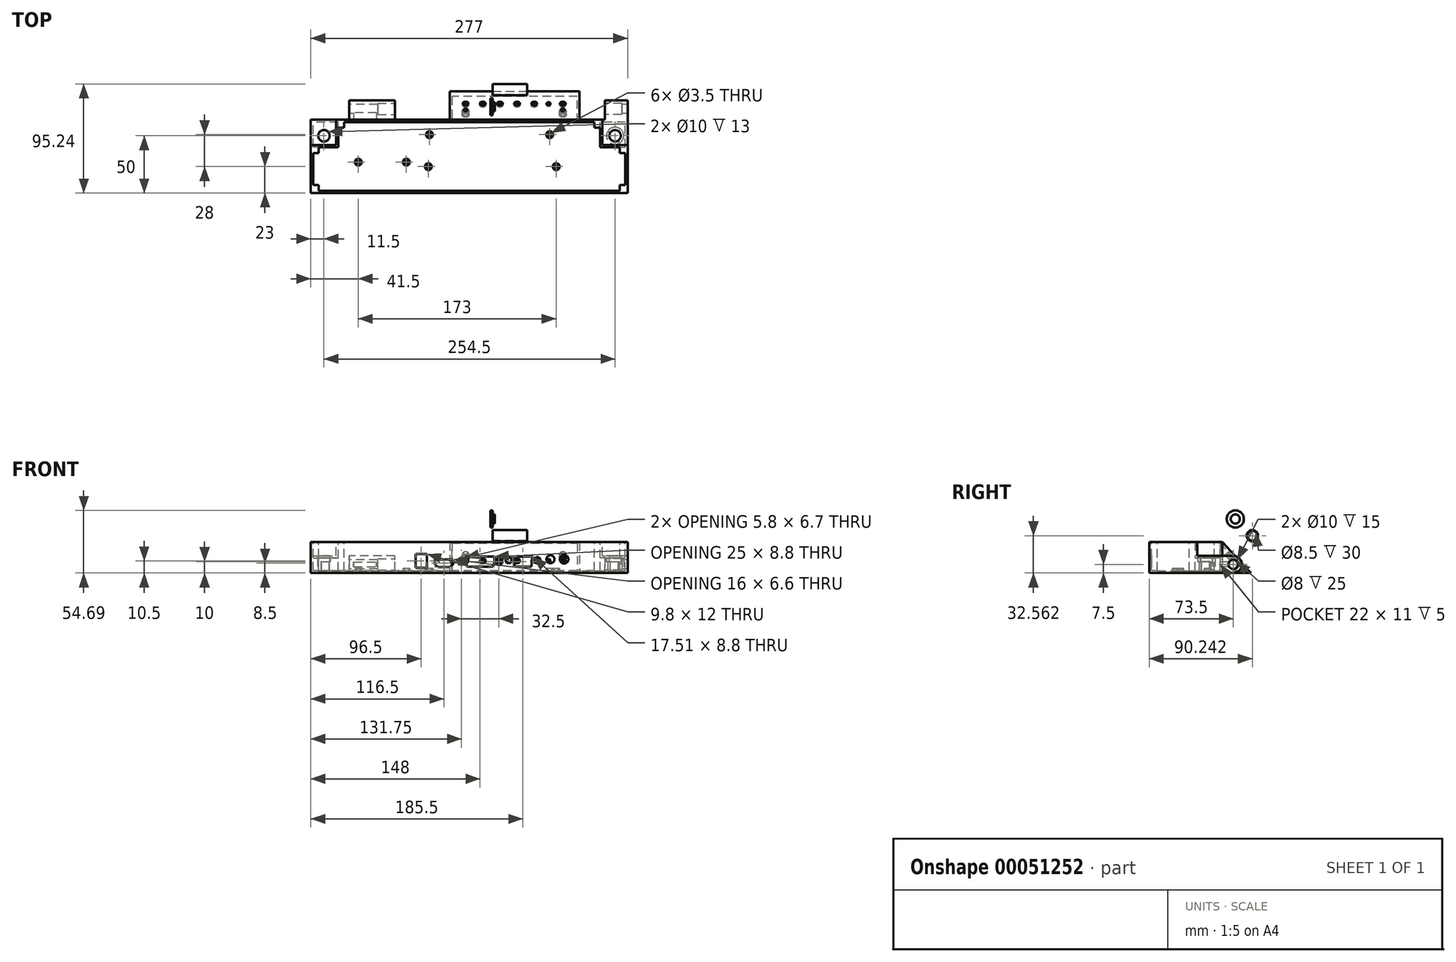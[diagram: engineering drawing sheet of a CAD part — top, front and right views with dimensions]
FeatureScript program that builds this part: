
annotation { "Feature Type Name" : "Feature", "Feature Type Description" : "" }
export const myFeature = defineFeature(function(context is Context, id is Id, definition is map)
    precondition{}
    {
        {
            var Q0;
            Q0=qCreatedBy(makeId("Top.planeOp"),FACE);
            var sketch = newSketch(context, id + "F0", { "sketchPlane" : qUnion([Q0])});
            skLineSegment(sketch, "E0.rect.bottom", {"start": v(69.5, 29) * mm, "end": v(-69.5, 29) * mm, "construction": true});
            skLineSegment(sketch, "E0.rect.top", {"start": v(69.5, -29) * mm, "end": v(-69.5, -29) * mm, "construction": true});
            skLineSegment(sketch, "E0.rect.left", {"start": v(69.5, 29) * mm, "end": v(69.5, -29) * mm, "construction": true});
            skLineSegment(sketch, "E0.rect.right", {"start": v(-69.5, 29) * mm, "end": v(-69.5, -29) * mm, "construction": true});
            skPoint(sketch, "E0.rect.middle", {"position": v(0, 0) * mm});
            skCircle(sketch, "E1", {"center": v(-56.2, -8) * mm, "radius": 1.75 * mm});
            skCircle(sketch, "E2", {"center": v(-55.2, 20) * mm, "radius": 1.75 * mm});
            skCircle(sketch, "E3", {"center": v(49.8, 20) * mm, "radius": 1.75 * mm});
            skCircle(sketch, "E4", {"center": v(55.5, -8) * mm, "radius": 1.75 * mm});
            skLineSegment(sketch, "E5", {"start": v(-69.27, -8) * mm, "end": v(180.27, -8) * mm, "construction": true});
            skLineSegment(sketch, "E6", {"start": v(-86.62, 20) * mm, "end": v(186.22, 20) * mm, "construction": true});
            skCircle(sketch, "E7.MirrorC", {"center": v(-117.5, -4) * mm, "radius": 1.75 * mm});
            skCircle(sketch, "E8.MirrorC", {"center": v(-75.5, -4) * mm, "radius": 1.75 * mm});
            skLineSegment(sketch, "E9.MirrorCS", {"start": v(-121.5, 29) * mm, "end": v(-71.5, 29) * mm, "construction": true});
            skLineSegment(sketch, "E10.MirrorCS", {"start": v(-121.5, -8) * mm, "end": v(-121.5, 29) * mm, "construction": true});
            skLineSegment(sketch, "E11.MirrorCS", {"start": v(-71.5, -8) * mm, "end": v(-71.5, 29) * mm, "construction": true});
            skLineSegment(sketch, "E12.MirrorCS", {"start": v(-121.5, -8) * mm, "end": v(-71.5, -8) * mm, "construction": true});
            skLineSegment(sketch, "E13.bottom", {"start": v(-125.5, 33) * mm, "end": v(73.5, 33) * mm});
            skLineSegment(sketch, "E13.top", {"start": v(-125.5, -31) * mm, "end": v(73.5, -31) * mm});
            skLineSegment(sketch, "E13.left", {"start": v(-125.5, 33) * mm, "end": v(-125.5, -31) * mm});
            skLineSegment(sketch, "E13.right", {"start": v(73.5, 33) * mm, "end": v(73.5, -31) * mm, "construction": true});
            skLineSegment(sketch, "E14", {"start": v(73.5, 33) * mm, "end": v(118, 33) * mm});
            skLineSegment(sketch, "E15", {"start": v(118, 33) * mm, "end": v(118, -31) * mm});
            skLineSegment(sketch, "E16", {"start": v(118, -31) * mm, "end": v(73.5, -31) * mm});
            skSolve(sketch);
        }
        {
            var Q0;
            Q0 = qSketchRegion(id + "F0", true);
            extrude(context, id + "F1", {"entities" : qUnion([Q0]), "depth" : 2 * mm});
        }
        {
            var Q0;
            Q0=makeQuery(id+"F1.opExtrude","CAP_FACE",FACE,{"disambiguationData":[OSD([sQuery(id+"F0.wireOp",EDGE,"E1"),sQuery(id+"F0.wireOp",EDGE,"E2"),sQuery(id+"F0.wireOp",EDGE,"E3"),sQuery(id+"F0.wireOp",EDGE,"E4"),sQuery(id+"F0.wireOp",EDGE,"E7.MirrorC"),sQuery(id+"F0.wireOp",EDGE,"E8.MirrorC"),sQuery(id+"F0.wireOp",EDGE,"E13.bottom"),sQuery(id+"F0.wireOp",EDGE,"E13.top"),sQuery(id+"F0.wireOp",EDGE,"E13.left"),sQuery(id+"F0.wireOp",EDGE,"E13.right")])],"isStart":false});
            var sketch = newSketch(context, id + "F2", { "sketchPlane" : qUnion([Q0])});
            skLineSegment(sketch, "E17.0.0", {"start": v(118, 33) * mm, "end": v(-125.5, 33) * mm});
            skLineSegment(sketch, "E17.0.1", {"start": v(-125.5, 33) * mm, "end": v(-125.5, -31) * mm});
            skLineSegment(sketch, "E17.0.2", {"start": v(-125.5, -31) * mm, "end": v(118, -31) * mm});
            skLineSegment(sketch, "E17.0.3", {"start": v(118, -31) * mm, "end": v(118, 33) * mm});
            skLineSegment(sketch, "E18.0", {"start": v(116, 31) * mm, "end": v(-123.5, 31) * mm});
            skLineSegment(sketch, "E18.1", {"start": v(116, -29) * mm, "end": v(116, 31) * mm});
            skLineSegment(sketch, "E18.2", {"start": v(-123.5, -29) * mm, "end": v(116, -29) * mm});
            skLineSegment(sketch, "E18.3", {"start": v(-123.5, 31) * mm, "end": v(-123.5, -29) * mm});
            skSolve(sketch);
        }
        {
            var Q0;
            Q0 = qSketchRegion(id + "F2", true);
            extrude(context, id + "F3", {"entities" : qUnion([Q0]), "operationType" : NewBodyOperationType.ADD, "depth" : 25 * mm});
        }
        {
            var Q0;
            Q0=makeQuery(id+"F3.boolean.opBoolean","MERGE",FACE,{"derivedFrom":[makeQuery(id+"F1.opExtrude","SWEPT_FACE",FACE,{"disambiguationData":[OSD([sQuery(id+"F0.wireOp",EDGE,"E13.left")])]}),makeQuery(id+"F3.opExtrude","SWEPT_FACE",FACE,{"disambiguationData":[OSD([sQuery(id+"F2.wireOp",EDGE,"1c2f05f6-80d2-497f-b791-f767546df5bb.0.1")])]})]});
            var sketch = newSketch(context, id + "F4", { "sketchPlane" : qUnion([Q0])});
            skLineSegment(sketch, "E19", {"start": v(-33, 0) * mm, "end": v(-43.93, 0) * mm, "construction": true});
            skLineSegment(sketch, "E20", {"start": v(-35, 0) * mm, "end": v(-35, 12.21) * mm, "construction": true});
            skCircle(sketch, "E21", {"center": v(-42.5, 7.5) * mm, "radius": 7.5 * mm});
            skLineSegment(sketch, "E22", {"start": v(-42.5, 15) * mm, "end": v(-33, 15) * mm});
            skLineSegment(sketch, "E23", {"start": v(-42.5, 0) * mm, "end": v(-33, 0) * mm});
            skLineSegment(sketch, "E24", {"start": v(-33, 0) * mm, "end": v(-33, 15) * mm});
            skCircle(sketch, "E25", {"center": v(-42.5, 7.5) * mm, "radius": 4 * mm});
            skSolve(sketch);
        }
        {
            var Q0;
            {var subQ0=sQuery(id+"F4.wireOp",EDGE,"E22");Q0=makeQuery(id+"F4.imprint","IMPRINT",FACE,{"disambiguationData":[TD([[makeQuery(id+"F4.imprint","IMPRINT",EDGE,{"derivedFrom":subQ0}),-1.0]])]});}
            var Q1;
            Q1=makeQuery(id+"F4.imprint","IMPRINT",FACE,{"disambiguationData":[TD([[makeQuery(id+"F4.imprint","IMPRINT",EDGE,{"derivedFrom":sQuery(id+"F4.wireOp",EDGE,"E25")}),-1.0]])]});
            var Q2;
            Q2=makeQuery(id+"F3.boolean.opBoolean","MERGE",FACE,{"derivedFrom":[makeQuery(id+"F1.opExtrude","SWEPT_FACE",FACE,{"disambiguationData":[OSD([sQuery(id+"F0.wireOp",EDGE,"E15")])]}),makeQuery(id+"F3.opExtrude","SWEPT_FACE",FACE,{"disambiguationData":[OSD([sQuery(id+"F2.wireOp",EDGE,"E17.0.3")])]})]});
            extrude(context, id + "F5", {"entities" : qUnion([Q0, Q1]), "operationType" : NewBodyOperationType.ADD, "endBound" : BoundingType.UP_TO_SURFACE, "oppositeDirection" : true, "endBoundEntityFace" : qUnion([Q2]), "depth" : 243.5 * mm});
        }
        {
            var Q0;
            Q0=makeQuery(id+"F5.opExtrude","SWEPT_FACE",FACE,{"disambiguationData":[OSD([sQuery(id+"F4.wireOp",EDGE,"E22")])]});
            var sketch = newSketch(context, id + "F6", { "sketchPlane" : qUnion([Q0])});
            skLineSegment(sketch, "E26.bottom", {"start": v(98, 33) * mm, "end": v(-85.5, 33) * mm});
            skLineSegment(sketch, "E26.top", {"start": v(98, 66.41) * mm, "end": v(-85.5, 66.41) * mm});
            skLineSegment(sketch, "E26.left", {"start": v(98, 33) * mm, "end": v(98, 66.41) * mm});
            skLineSegment(sketch, "E26.right", {"start": v(-85.5, 33) * mm, "end": v(-85.5, 66.41) * mm});
            skSolve(sketch);
        }
        {
            var Q0;
            {var subQ0=sQuery(id+"F6.wireOp",EDGE,"E26.top");Q0=makeQuery(id+"F6.imprint","IMPRINT",FACE,{"disambiguationData":[TD([[makeQuery(id+"F6.imprint","IMPRINT",EDGE,{"derivedFrom":subQ0}),1.0]])]});}
            var Q1;
            {var subQ0=sQuery(id+"F6.wireOp",EDGE,"E26.bottom");Q1=makeQuery(id+"F6.imprint","IMPRINT",FACE,{"disambiguationData":[TD([[makeQuery(id+"F6.imprint","IMPRINT",EDGE,{"derivedFrom":subQ0}),-1.0]])]});}
            extrude(context, id + "F7", {"entities" : qUnion([Q0, Q1]), "operationType" : NewBodyOperationType.REMOVE, "endBound" : BoundingType.THROUGH_ALL, "oppositeDirection" : true, "depth" : 25 * mm});
        }
        {
            var Q0;
            Q0=qCreatedBy(makeId("Right.planeOp"),FACE);
            var sketch = newSketch(context, id + "F8", { "sketchPlane" : qUnion([Q0])});
            skCircle(sketch, "E27", {"center": v(59.24, 32.56) * mm, "radius": 5 * mm});
            skCircle(sketch, "E28", {"center": v(59.24, 32.56) * mm, "radius": 4.25 * mm});
            skSolve(sketch);
        }
        {
            var Q0;
            Q0 = qSketchRegion(id + "F8", true);
            extrude(context, id + "F9", {"entities" : qUnion([Q0]), "depth" : 30 * mm});
        }
        {
            var Q0;
            Q0=qCreatedBy(makeId("Right.planeOp"),FACE);
            var sketch = newSketch(context, id + "F10", { "sketchPlane" : qUnion([Q0])});
            skCircle(sketch, "E29", {"center": v(44.32, 47.2) * mm, "radius": 7.5 * mm});
            skCircle(sketch, "E30", {"center": v(44.32, 47.2) * mm, "radius": 4 * mm});
            skSolve(sketch);
        }
        {
            var Q0;
            Q0=makeQuery(id+"F10.imprint","IMPRINT",FACE,{"disambiguationData":[TD([[makeQuery(id+"F10.imprint","IMPRINT",EDGE,{"derivedFrom":sQuery(id+"F10.wireOp",EDGE,"E29")}),1.0]])]});
            var Q1;
            Q1=makeQuery(id+"F10.imprint","IMPRINT",FACE,{"disambiguationData":[TD([[makeQuery(id+"F10.imprint","IMPRINT",EDGE,{"derivedFrom":sQuery(id+"F10.wireOp",EDGE,"E30")}),1.0]])]});
            extrude(context, id + "F11", {"entities" : qUnion([Q0, Q1]), "oppositeDirection" : true, "depth" : 2 * mm});
        }
        {
            var Q0;
            Q0=makeQuery(id+"F10.imprint","IMPRINT",FACE,{"disambiguationData":[TD([[makeQuery(id+"F10.imprint","IMPRINT",EDGE,{"derivedFrom":sQuery(id+"F10.wireOp",EDGE,"E30")}),1.0]])]});
            extrude(context, id + "F12", {"entities" : qUnion([Q0]), "operationType" : NewBodyOperationType.ADD, "depth" : 2 * mm});
        }
        {
            var Q0;
            Q0=makeQuery(id+"F1.opExtrude","CAP_FACE",FACE,{"disambiguationData":[OSD([sQuery(id+"F0.wireOp",EDGE,"E1"),sQuery(id+"F0.wireOp",EDGE,"E2"),sQuery(id+"F0.wireOp",EDGE,"E3"),sQuery(id+"F0.wireOp",EDGE,"E4"),sQuery(id+"F0.wireOp",EDGE,"E7.MirrorC"),sQuery(id+"F0.wireOp",EDGE,"E8.MirrorC"),sQuery(id+"F0.wireOp",EDGE,"E13.bottom"),sQuery(id+"F0.wireOp",EDGE,"E13.top"),sQuery(id+"F0.wireOp",EDGE,"E13.left"),sQuery(id+"F0.wireOp",EDGE,"E13.right")])],"isStart":false});
            var sketch = newSketch(context, id + "F13", { "sketchPlane" : qUnion([Q0])});
            skCircle(sketch, "E31", {"center": v(-117.5, -4) * mm, "radius": 3 * mm});
            skCircle(sketch, "E32", {"center": v(-75.5, -4) * mm, "radius": 3 * mm});
            skCircle(sketch, "E33", {"center": v(-56.2, -8) * mm, "radius": 3 * mm});
            skCircle(sketch, "E34", {"center": v(-55.2, 20) * mm, "radius": 3 * mm});
            skCircle(sketch, "E35", {"center": v(49.8, 20) * mm, "radius": 3 * mm});
            skCircle(sketch, "E36", {"center": v(55.5, -8) * mm, "radius": 3 * mm});
            skCircle(sketch, "E37.0", {"center": v(-117.5, -4) * mm, "radius": 1.75 * mm});
            skCircle(sketch, "E38.0", {"center": v(-75.5, -4) * mm, "radius": 1.75 * mm});
            skCircle(sketch, "E39.0", {"center": v(-55.2, 20) * mm, "radius": 1.75 * mm});
            skCircle(sketch, "E40.0", {"center": v(-56.2, -8) * mm, "radius": 1.75 * mm});
            skCircle(sketch, "E41.0", {"center": v(49.8, 20) * mm, "radius": 1.75 * mm});
            skCircle(sketch, "E42.0", {"center": v(55.5, -8) * mm, "radius": 1.75 * mm});
            skSolve(sketch);
        }
        {
            var Q0;
            Q0 = qSketchRegion(id + "F13", true);
            extrude(context, id + "F14", {"entities" : qUnion([Q0]), "operationType" : NewBodyOperationType.ADD, "depth" : 2 * mm});
        }
        {
            var Q0;
            Q0=makeQuery(id+"F3.opExtrude","SWEPT_FACE",FACE,{"disambiguationData":[OSD([sQuery(id+"F2.wireOp",EDGE,"E18.0")])]});
            var sketch = newSketch(context, id + "F15", { "sketchPlane" : qUnion([Q0])});
            skLineSegment(sketch, "E43.bottom", {"start": v(-121.5, 9.5) * mm, "end": v(-101.5, 9.5) * mm});
            skLineSegment(sketch, "E43.top", {"start": v(-121.5, 5.5) * mm, "end": v(-101.5, 5.5) * mm});
            skLineSegment(sketch, "E43.left", {"start": v(-121.5, 9.5) * mm, "end": v(-121.5, 5.5) * mm});
            skLineSegment(sketch, "E43.right", {"start": v(-101.5, 9.5) * mm, "end": v(-101.5, 5.5) * mm});
            skSolve(sketch);
        }
        {
            var Q0;
            Q0 = qSketchRegion(id + "F15", true);
            extrude(context, id + "F16", {"entities" : qUnion([Q0]), "operationType" : NewBodyOperationType.REMOVE, "endBound" : BoundingType.SYMMETRIC, "oppositeDirection" : true, "depth" : 25 * mm});
        }
        {
            var Q0;
            Q0=makeQuery(id+"F7.boolean.opBoolean","COPY",FACE,{"derivedFrom":makeQuery(id+"F7.opExtrude","SWEPT_FACE",FACE,{"disambiguationData":[OSD([sQuery(id+"F6.wireOp",EDGE,"E26.left")])]})});
            var sketch = newSketch(context, id + "F17", { "sketchPlane" : qUnion([Q0])});
            skCircle(sketch, "E44", {"center": v(-42.5, 7.5) * mm, "radius": 5 * mm});
            skSolve(sketch);
        }
        {
            var Q0;
            Q0 = qSketchRegion(id + "F17", true);
            extrude(context, id + "F18", {"entities" : qUnion([Q0]), "operationType" : NewBodyOperationType.REMOVE, "oppositeDirection" : true, "depth" : 15 * mm});
        }
        {
            var Q0;
            Q0=makeQuery(id+"F7.boolean.opBoolean","COPY",FACE,{"derivedFrom":makeQuery(id+"F7.opExtrude","SWEPT_FACE",FACE,{"disambiguationData":[OSD([sQuery(id+"F6.wireOp",EDGE,"E26.right")])]})});
            var sketch = newSketch(context, id + "F19", { "sketchPlane" : qUnion([Q0])});
            skCircle(sketch, "E45", {"center": v(42.5, 7.5) * mm, "radius": 5 * mm});
            skSolve(sketch);
        }
        {
            var Q0;
            Q0 = qSketchRegion(id + "F19", true);
            extrude(context, id + "F20", {"entities" : qUnion([Q0]), "operationType" : NewBodyOperationType.REMOVE, "oppositeDirection" : true, "depth" : 15 * mm});
        }
        {
            var Q0;
            Q0=makeQuery(id+"F3.opExtrude","CAP_FACE",FACE,{"disambiguationData":[OSD([sQuery(id+"F2.wireOp",EDGE,"E17.0.0"),sQuery(id+"F2.wireOp",EDGE,"E17.0.1"),sQuery(id+"F2.wireOp",EDGE,"E17.0.2"),sQuery(id+"F2.wireOp",EDGE,"E17.0.3"),sQuery(id+"F2.wireOp",EDGE,"E18.0"),sQuery(id+"F2.wireOp",EDGE,"E18.1"),sQuery(id+"F2.wireOp",EDGE,"E18.2"),sQuery(id+"F2.wireOp",EDGE,"E18.3")])],"isStart":false});
            var sketch = newSketch(context, id + "F21", { "sketchPlane" : qUnion([Q0])});
            skPoint(sketch, "E46.0", {"position": v(-125.5, 33) * mm});
            skPoint(sketch, "E47.0", {"position": v(-125.5, -31) * mm});
            skLineSegment(sketch, "E48", {"start": v(-125.5, -31) * mm, "end": v(-159, -31) * mm});
            skLineSegment(sketch, "E49", {"start": v(-159, -31) * mm, "end": v(-159, 33) * mm});
            skLineSegment(sketch, "E50", {"start": v(-159, 33) * mm, "end": v(-125.5, 33) * mm});
            skLineSegment(sketch, "E51", {"start": v(-125.5, -31) * mm, "end": v(-125.5, 33) * mm});
            skSolve(sketch);
        }
        {
            var Q0;
            Q0 = qSketchRegion(id + "F21", true);
            var Q1;
            Q1=makeQuery(id+"F5.boolean.opBoolean","MERGE",FACE,{"derivedFrom":[makeQuery(id+"F1.opExtrude","CAP_FACE",FACE,{"disambiguationData":[OSD([sQuery(id+"F0.wireOp",EDGE,"E1"),sQuery(id+"F0.wireOp",EDGE,"E2"),sQuery(id+"F0.wireOp",EDGE,"E3"),sQuery(id+"F0.wireOp",EDGE,"E4"),sQuery(id+"F0.wireOp",EDGE,"E7.MirrorC"),sQuery(id+"F0.wireOp",EDGE,"E8.MirrorC"),sQuery(id+"F0.wireOp",EDGE,"E13.bottom"),sQuery(id+"F0.wireOp",EDGE,"E13.top"),sQuery(id+"F0.wireOp",EDGE,"E13.left"),sQuery(id+"F0.wireOp",EDGE,"E14"),sQuery(id+"F0.wireOp",EDGE,"E15"),sQuery(id+"F0.wireOp",EDGE,"E16")])],"isStart":true}),makeQuery(id+"F5.opExtrude","SWEPT_FACE",FACE,{"disambiguationData":[OSD([sQuery(id+"F4.wireOp",EDGE,"E23")])]})]});
            extrude(context, id + "F22", {"entities" : qUnion([Q0]), "operationType" : NewBodyOperationType.ADD, "endBound" : BoundingType.UP_TO_SURFACE, "oppositeDirection" : true, "endBoundEntityFace" : qUnion([Q1]), "depth" : 25 * mm});
        }
        {
            var Q0;
            Q0=makeQuery(id+"F22.boolean.opBoolean","MERGE",FACE,{"derivedFrom":[makeQuery(id+"F3.opExtrude","CAP_FACE",FACE,{"disambiguationData":[OSD([sQuery(id+"F2.wireOp",EDGE,"E17.0.0"),sQuery(id+"F2.wireOp",EDGE,"E17.0.1"),sQuery(id+"F2.wireOp",EDGE,"E17.0.2"),sQuery(id+"F2.wireOp",EDGE,"E17.0.3"),sQuery(id+"F2.wireOp",EDGE,"E18.0"),sQuery(id+"F2.wireOp",EDGE,"E18.1"),sQuery(id+"F2.wireOp",EDGE,"E18.2"),sQuery(id+"F2.wireOp",EDGE,"E18.3")])],"isStart":false}),makeQuery(id+"F22.opExtrude","CAP_FACE",FACE,{"disambiguationData":[OSD([sQuery(id+"F21.wireOp",EDGE,"E48"),sQuery(id+"F21.wireOp",EDGE,"E49"),sQuery(id+"F21.wireOp",EDGE,"E50"),sQuery(id+"F21.wireOp",EDGE,"E51")])],"isStart":true})]});
            var sketch = newSketch(context, id + "F23", { "sketchPlane" : qUnion([Q0])});
            skLineSegment(sketch, "E52.bottom", {"start": v(-123.5, 31) * mm, "end": v(-157, 31) * mm});
            skLineSegment(sketch, "E52.top", {"start": v(-123.5, -29) * mm, "end": v(-157, -29) * mm});
            skLineSegment(sketch, "E52.left", {"start": v(-123.5, 31) * mm, "end": v(-123.5, -29) * mm});
            skLineSegment(sketch, "E52.right", {"start": v(-157, 31) * mm, "end": v(-157, -29) * mm});
            skSolve(sketch);
        }
        {
            var Q0;
            Q0 = qSketchRegion(id + "F23", true);
            var Q1;
            Q1=makeQuery(id+"F1.opExtrude","CAP_FACE",FACE,{"disambiguationData":[OSD([sQuery(id+"F0.wireOp",EDGE,"E1"),sQuery(id+"F0.wireOp",EDGE,"E2"),sQuery(id+"F0.wireOp",EDGE,"E3"),sQuery(id+"F0.wireOp",EDGE,"E4"),sQuery(id+"F0.wireOp",EDGE,"E7.MirrorC"),sQuery(id+"F0.wireOp",EDGE,"E8.MirrorC"),sQuery(id+"F0.wireOp",EDGE,"E13.bottom"),sQuery(id+"F0.wireOp",EDGE,"E13.top"),sQuery(id+"F0.wireOp",EDGE,"E13.left"),sQuery(id+"F0.wireOp",EDGE,"E14"),sQuery(id+"F0.wireOp",EDGE,"E15"),sQuery(id+"F0.wireOp",EDGE,"E16")])],"isStart":false});
            extrude(context, id + "F24", {"entities" : qUnion([Q0]), "operationType" : NewBodyOperationType.REMOVE, "endBound" : BoundingType.UP_TO_SURFACE, "oppositeDirection" : true, "endBoundEntityFace" : qUnion([Q1]), "depth" : 25 * mm});
        }
        {
            var Q0;
            Q0=qCreatedBy(makeId("Top.planeOp"),FACE);
            var sketch = newSketch(context, id + "F25", { "sketchPlane" : qUnion([Q0])});
            skLineSegment(sketch, "E53.0", {"start": v(-159, 33) * mm, "end": v(118, 33) * mm, "construction": true});
            skLineSegment(sketch, "E54.bottom", {"start": v(-37.5, 33) * mm, "end": v(76, 33) * mm});
            skLineSegment(sketch, "E54.top", {"start": v(-37.5, 58) * mm, "end": v(76, 58) * mm});
            skLineSegment(sketch, "E54.left", {"start": v(-37.5, 33) * mm, "end": v(-37.5, 58) * mm});
            skLineSegment(sketch, "E54.right", {"start": v(76, 33) * mm, "end": v(76, 58) * mm});
            skSolve(sketch);
        }
        {
            var Q0;
            Q0 = qSketchRegion(id + "F25", true);
            var Q1;
            Q1=makeQuery(id+"F22.boolean.opBoolean","MERGE",FACE,{"derivedFrom":[makeQuery(id+"F3.opExtrude","CAP_FACE",FACE,{"disambiguationData":[OSD([sQuery(id+"F2.wireOp",EDGE,"E17.0.0"),sQuery(id+"F2.wireOp",EDGE,"E17.0.1"),sQuery(id+"F2.wireOp",EDGE,"E17.0.2"),sQuery(id+"F2.wireOp",EDGE,"E17.0.3"),sQuery(id+"F2.wireOp",EDGE,"E18.0"),sQuery(id+"F2.wireOp",EDGE,"E18.1"),sQuery(id+"F2.wireOp",EDGE,"E18.2"),sQuery(id+"F2.wireOp",EDGE,"E18.3")])],"isStart":false}),makeQuery(id+"F22.opExtrude","CAP_FACE",FACE,{"disambiguationData":[OSD([sQuery(id+"F21.wireOp",EDGE,"E48"),sQuery(id+"F21.wireOp",EDGE,"E49"),sQuery(id+"F21.wireOp",EDGE,"E50"),sQuery(id+"F21.wireOp",EDGE,"E51")])],"isStart":true})]});
            extrude(context, id + "F26", {"entities" : qUnion([Q0]), "operationType" : NewBodyOperationType.ADD, "endBound" : BoundingType.UP_TO_SURFACE, "endBoundEntityFace" : qUnion([Q1]), "depth" : 20 * mm});
        }
        {
            var Q0;
            Q0=makeQuery(id+"F26.opExtrude","SWEPT_FACE",FACE,{"disambiguationData":[OSD([sQuery(id+"F25.wireOp",EDGE,"E54.left")])]});
            var sketch = newSketch(context, id + "F27", { "sketchPlane" : qUnion([Q0])});
            skLineSegment(sketch, "E55.0", {"start": v(-33, 27) * mm, "end": v(-58, 27) * mm});
            skLineSegment(sketch, "E56.0", {"start": v(-58, 27) * mm, "end": v(-58, 0) * mm});
            skLineSegment(sketch, "E57", {"start": v(-58, 0) * mm, "end": v(-33, 27) * mm});
            skSolve(sketch);
        }
        {
            var Q0;
            Q0 = qSketchRegion(id + "F27", true);
            extrude(context, id + "F28", {"entities" : qUnion([Q0]), "operationType" : NewBodyOperationType.REMOVE, "endBound" : BoundingType.UP_TO_NEXT, "oppositeDirection" : true, "depth" : 25 * mm});
        }
        {
            var Q0;
            Q0=makeQuery(id+"F26.opExtrude","SWEPT_FACE",FACE,{"disambiguationData":[OSD([sQuery(id+"F25.wireOp",EDGE,"E54.left")])]});
            var sketch = newSketch(context, id + "F29", { "sketchPlane" : qUnion([Q0])});
            skLineSegment(sketch, "E58.0", {"start": v(-58, 0) * mm, "end": v(-33, 27) * mm});
            skLineSegment(sketch, "E59.0", {"start": v(-33, 0) * mm, "end": v(-33, 27) * mm});
            skLineSegment(sketch, "E60.0", {"start": v(-33, 0) * mm, "end": v(-58, 0) * mm});
            skLineSegment(sketch, "E61.0", {"start": v(-53.42, 2) * mm, "end": v(-35, 21.9) * mm});
            skLineSegment(sketch, "E61.1", {"start": v(-35, 2) * mm, "end": v(-53.42, 2) * mm});
            skLineSegment(sketch, "E61.2", {"start": v(-35, 2) * mm, "end": v(-35, 21.9) * mm});
            skLineSegment(sketch, "E62", {"start": v(-35, 21.9) * mm, "end": v(-26.5, 31.08) * mm});
            skLineSegment(sketch, "E63", {"start": v(-35, 2) * mm, "end": v(-26.5, 2) * mm});
            skLineSegment(sketch, "E64", {"start": v(-26.5, 2) * mm, "end": v(-26.5, 31.08) * mm});
            skSolve(sketch);
        }
        {
            var Q0;
            {var subQ5=sQuery(id+"F29.wireOp",EDGE,"E64");Q0=makeQuery(id+"F29.imprint","IMPRINT",FACE,{"disambiguationData":[TD([[makeQuery(id+"F29.imprint","IMPRINT",EDGE,{"derivedFrom":subQ5}),1.0]])]});}
            var Q1;
            Q1=makeQuery(id+"F29.imprint","IMPRINT",FACE,{"disambiguationData":[TD([[makeQuery(id+"F29.imprint","IMPRINT",EDGE,{"derivedFrom":sQuery(id+"F29.wireOp",EDGE,"E61.0")}),-1.0]])]});
            var Q2;
            {var subQ5=sQuery(id+"F29.wireOp",EDGE,"E61.2");Q2=makeQuery(id+"F29.imprint","IMPRINT",FACE,{"disambiguationData":[TD([[makeQuery(id+"F29.imprint","IMPRINT",EDGE,{"derivedFrom":subQ5}),-1.0]])]});}
            var Q3;
            Q3=makeQuery(id+"F26.opExtrude","SWEPT_FACE",FACE,{"disambiguationData":[OSD([sQuery(id+"F25.wireOp",EDGE,"E54.right")])]});
            extrude(context, id + "F30", {"entities" : qUnion([Q0, Q1, Q2]), "operationType" : NewBodyOperationType.REMOVE, "endBound" : BoundingType.UP_TO_SURFACE, "oppositeDirection" : true, "endBoundEntityFace" : qUnion([Q3]), "depth" : 25 * mm});
        }
        {
            var Q0;
            Q0=makeQuery(id+"F28.boolean.opBoolean","COPY",FACE,{"derivedFrom":makeQuery(id+"F28.opExtrude","SWEPT_FACE",FACE,{"disambiguationData":[OSD([sQuery(id+"F27.wireOp",EDGE,"E57")])]})});
            var sketch = newSketch(context, id + "F31", { "sketchPlane" : qUnion([Q0])});
            skPoint(sketch, "E65.0", {"position": v(-61.33, -15.4) * mm});
            skPoint(sketch, "E66.0", {"position": v(-61.33, -23.4) * mm});
            skPoint(sketch, "E67.0", {"position": v(-48.83, -23.4) * mm});
            skPoint(sketch, "E68.0", {"position": v(-36.33, -23.4) * mm});
            skPoint(sketch, "E69.0", {"position": v(-21.33, -23.4) * mm});
            skPoint(sketch, "E70.0", {"position": v(-6.33, -23.4) * mm});
            skPoint(sketch, "E71.0", {"position": v(8.67, -23.4) * mm});
            skPoint(sketch, "E72.0", {"position": v(23.67, -23.4) * mm});
            skPoint(sketch, "E73.0", {"position": v(23.67, -15.4) * mm});
            skCircle(sketch, "E74", {"center": v(-61.33, -15.4) * mm, "radius": 1.75 * mm});
            skCircle(sketch, "E75", {"center": v(-61.33, -23.4) * mm, "radius": 2.5 * mm});
            skCircle(sketch, "E76", {"center": v(-48.83, -23.4) * mm, "radius": 1.75 * mm});
            skCircle(sketch, "E77", {"center": v(-36.33, -23.4) * mm, "radius": 2.5 * mm});
            skCircle(sketch, "E78", {"center": v(-21.33, -23.4) * mm, "radius": 2.5 * mm});
            skCircle(sketch, "E79", {"center": v(-6.33, -23.4) * mm, "radius": 2.5 * mm});
            skCircle(sketch, "E80", {"center": v(8.67, -23.4) * mm, "radius": 2.5 * mm});
            skCircle(sketch, "E81", {"center": v(23.67, -23.4) * mm, "radius": 2.5 * mm});
            skCircle(sketch, "E82", {"center": v(23.67, -15.4) * mm, "radius": 1.75 * mm});
            skLineSegment(sketch, "E83", {"start": v(-61.33, -23.4) * mm, "end": v(23.67, -23.4) * mm, "construction": true});
            skLineSegment(sketch, "E84", {"start": v(23.67, -15.4) * mm, "end": v(-61.33, -15.4) * mm, "construction": true});
            skSolve(sketch);
        }
        {
            var Q0;
            Q0 = qSketchRegion(id + "F31", true);
            extrude(context, id + "F32", {"entities" : qUnion([Q0]), "operationType" : NewBodyOperationType.REMOVE, "endBound" : BoundingType.UP_TO_NEXT, "oppositeDirection" : true, "depth" : 25 * mm});
        }
        {
            var Q0;
            Q0=makeQuery(id+"F30.boolean.opBoolean","COPY",FACE,{"derivedFrom":makeQuery(id+"F30.opExtrude","SWEPT_FACE",FACE,{"disambiguationData":[OSD([sQuery(id+"F29.wireOp",EDGE,"E61.0"),sQuery(id+"F29.wireOp",EDGE,"E62")])]})});
            var sketch = newSketch(context, id + "F33", { "sketchPlane" : qUnion([Q0])});
            skCircle(sketch, "E85.0", {"center": v(61.33, -15.4) * mm, "radius": 1.75 * mm});
            skCircle(sketch, "E86.0", {"center": v(-23.67, -15.4) * mm, "radius": 1.75 * mm});
            skCircle(sketch, "E87", {"center": v(-23.67, -15.4) * mm, "radius": 3 * mm});
            skCircle(sketch, "E88", {"center": v(61.33, -15.4) * mm, "radius": 3 * mm});
            skSolve(sketch);
        }
        {
            var Q0;
            Q0 = qSketchRegion(id + "F33", true);
            extrude(context, id + "F34", {"entities" : qUnion([Q0]), "operationType" : NewBodyOperationType.ADD, "depth" : 4 * mm});
        }
        {
            var Q0;
            Q0=makeQuery(id+"F30.boolean.opBoolean","COPY",FACE,{"derivedFrom":makeQuery(id+"F30.opExtrude","CAP_FACE",FACE,{"disambiguationData":[OSD([sQuery(id+"F29.wireOp",EDGE,"E61.0"),sQuery(id+"F29.wireOp",EDGE,"E61.1"),sQuery(id+"F29.wireOp",EDGE,"E62"),sQuery(id+"F29.wireOp",EDGE,"E63"),sQuery(id+"F29.wireOp",EDGE,"E64")])],"isStart":true})});
            var sketch = newSketch(context, id + "F35", { "sketchPlane" : qUnion([Q0])});
            skLineSegment(sketch, "E89.0", {"start": v(33, 24.06) * mm, "end": v(31, 26.22) * mm});
            skLineSegment(sketch, "E90.0", {"start": v(53.42, 2) * mm, "end": v(33, 24.06) * mm});
            skLineSegment(sketch, "E91.0", {"start": v(31, 26.22) * mm, "end": v(31, 2) * mm});
            skLineSegment(sketch, "E92.0", {"start": v(33, 2) * mm, "end": v(31, 2) * mm});
            skLineSegment(sketch, "E93.0", {"start": v(53.42, 2) * mm, "end": v(33, 2) * mm});
            skSolve(sketch);
        }
        {
            var Q0;
            Q0 = qSketchRegion(id + "F35", true);
            extrude(context, id + "F36", {"entities" : qUnion([Q0]), "operationType" : NewBodyOperationType.ADD, "depth" : 2 * mm});
        }
        {
            var Q0;
            Q0=makeQuery(id+"F30.boolean.opBoolean","COPY",FACE,{"derivedFrom":makeQuery(id+"F30.opExtrude","CAP_FACE",FACE,{"disambiguationData":[OSD([sQuery(id+"F29.wireOp",EDGE,"E61.0"),sQuery(id+"F29.wireOp",EDGE,"E61.1"),sQuery(id+"F29.wireOp",EDGE,"E62"),sQuery(id+"F29.wireOp",EDGE,"E63"),sQuery(id+"F29.wireOp",EDGE,"E64")])],"isStart":false})});
            var sketch = newSketch(context, id + "F37", { "sketchPlane" : qUnion([Q0])});
            skLineSegment(sketch, "E94.0", {"start": v(-33, 24.06) * mm, "end": v(-53.42, 2) * mm});
            skLineSegment(sketch, "E95.0", {"start": v(-31, 26.22) * mm, "end": v(-33, 24.06) * mm});
            skLineSegment(sketch, "E96.0", {"start": v(-31, 26.22) * mm, "end": v(-31, 2) * mm});
            skLineSegment(sketch, "E97.0", {"start": v(-33, 2) * mm, "end": v(-53.42, 2) * mm});
            skLineSegment(sketch, "E98.0", {"start": v(-31, 2) * mm, "end": v(-33, 2) * mm});
            skSolve(sketch);
        }
        {
            var Q0;
            Q0 = qSketchRegion(id + "F37", true);
            extrude(context, id + "F38", {"entities" : qUnion([Q0]), "operationType" : NewBodyOperationType.ADD, "depth" : 2 * mm});
        }
        {
            var Q0;
            Q0=makeQuery(id+"F22.boolean.opBoolean","MERGE",FACE,{"derivedFrom":[makeQuery(id+"F3.boolean.opBoolean","MERGE",FACE,{"derivedFrom":[makeQuery(id+"F1.opExtrude","SWEPT_FACE",FACE,{"disambiguationData":[OSD([sQuery(id+"F0.wireOp",EDGE,"E13.top"),sQuery(id+"F0.wireOp",EDGE,"E16")])]}),makeQuery(id+"F3.opExtrude","SWEPT_FACE",FACE,{"disambiguationData":[OSD([sQuery(id+"F2.wireOp",EDGE,"E17.0.2")])]})]}),makeQuery(id+"F22.opExtrude","SWEPT_FACE",FACE,{"disambiguationData":[OSD([sQuery(id+"F21.wireOp",EDGE,"E48")])]})]});
            var sketch = newSketch(context, id + "F39", { "sketchPlane" : qUnion([Q0])});
            skPoint(sketch, "E99", {"position": v(-159, 27) * mm});
            skLineSegment(sketch, "E100.0", {"start": v(19.85, 6.1) * mm, "end": v(33.15, 6.1) * mm});
            skLineSegment(sketch, "E101.0", {"start": v(-58.1, 16) * mm, "end": v(-58.1, 5) * mm});
            skLineSegment(sketch, "E102.0", {"start": v(-58.1, 16) * mm, "end": v(-66.9, 16) * mm});
            skLineSegment(sketch, "E103.0", {"start": v(-58.1, 5) * mm, "end": v(-66.9, 5) * mm});
            skLineSegment(sketch, "E104.0", {"start": v(-66.9, 16) * mm, "end": v(-66.9, 5) * mm});
            skLineSegment(sketch, "E105.0", {"start": v(-35, 11.3) * mm, "end": v(-50, 11.3) * mm});
            skLineSegment(sketch, "E106.0", {"start": v(-37.5, 5.7) * mm, "end": v(-47.5, 5.7) * mm});
            skLineSegment(sketch, "E107.0.1", {"start": v(69.5, 3.8) * mm, "end": v(69.5, 27) * mm});
            skLineSegment(sketch, "E107.0.0", {"start": v(-159, 3.8) * mm, "end": v(69.5, 3.8) * mm});
            skLineSegment(sketch, "E107.0.3", {"start": v(-159, 27) * mm, "end": v(-159, 3.8) * mm});
            skLineSegment(sketch, "E107.0.2", {"start": v(69.5, 27) * mm, "end": v(-159, 27) * mm});
            skCircle(sketch, "E108.0", {"center": v(62.5, 12) * mm, "radius": 3.25 * mm});
            skLineSegment(sketch, "E109.0", {"start": v(-23, 13.9) * mm, "end": v(1, 13.9) * mm});
            skLineSegment(sketch, "E110.0", {"start": v(18.35, 13.9) * mm, "end": v(34.65, 13.9) * mm});
            skLineSegment(sketch, "E111.0", {"start": v(-22, 6.1) * mm, "end": v(0, 6.1) * mm});
            skCircle(sketch, "E112.0", {"center": v(50.5, 12) * mm, "radius": 3 * mm});
            skLineSegment(sketch, "E113.0", {"start": v(1, 13.9) * mm, "end": v(1, 9.3) * mm});
            skLineSegment(sketch, "E114.0", {"start": v(34.65, 13.9) * mm, "end": v(33.15, 6.1) * mm});
            skLineSegment(sketch, "E115.0", {"start": v(5.25, 12.77) * mm, "end": v(2.85, 11.39) * mm});
            skLineSegment(sketch, "E116.0", {"start": v(37, 10.15) * mm, "end": v(39, 9) * mm});
            skLineSegment(sketch, "E117.2", {"start": v(-27.25, 7.23) * mm, "end": v(-29.65, 8.61) * mm});
            skLineSegment(sketch, "E118.0", {"start": v(-50, 7.53) * mm, "end": v(-50, 11.3) * mm});
            skLineSegment(sketch, "E119.0", {"start": v(-47.5, 5.7) * mm, "end": v(-50, 7.53) * mm});
            skLineSegment(sketch, "E120.0", {"start": v(-29.65, 8.61) * mm, "end": v(-29.65, 11.39) * mm});
            skLineSegment(sketch, "E121.0", {"start": v(-37.5, 5.7) * mm, "end": v(-35, 7.53) * mm});
            skLineSegment(sketch, "E122.0", {"start": v(-35, 7.53) * mm, "end": v(-35, 11.3) * mm});
            skLineSegment(sketch, "E123.0", {"start": v(12, 12.45) * mm, "end": v(14, 13.6) * mm});
            skLineSegment(sketch, "E124.0", {"start": v(-24.85, 11.39) * mm, "end": v(-24.85, 8.61) * mm});
            skLineSegment(sketch, "E125.0", {"start": v(12, 10.15) * mm, "end": v(12, 12.45) * mm});
            skLineSegment(sketch, "E126.0", {"start": v(-27.25, 12.77) * mm, "end": v(-24.85, 11.39) * mm});
            skLineSegment(sketch, "E127.0", {"start": v(-23, 13.9) * mm, "end": v(-23, 9.3) * mm});
            skLineSegment(sketch, "E128.0", {"start": v(-24.85, 8.61) * mm, "end": v(-27.25, 7.23) * mm});
            skLineSegment(sketch, "E129.0", {"start": v(18.35, 13.9) * mm, "end": v(19.85, 6.1) * mm});
            skLineSegment(sketch, "E130.0", {"start": v(-23, 9.3) * mm, "end": v(-22, 6.1) * mm});
            skLineSegment(sketch, "E131.0", {"start": v(5.25, 7.23) * mm, "end": v(7.65, 8.61) * mm});
            skLineSegment(sketch, "E132.0", {"start": v(39, 9) * mm, "end": v(41, 10.15) * mm});
            skLineSegment(sketch, "E133.0", {"start": v(-29.65, 11.39) * mm, "end": v(-27.25, 12.77) * mm});
            skLineSegment(sketch, "E134.0", {"start": v(1, 9.3) * mm, "end": v(0, 6.1) * mm});
            skLineSegment(sketch, "E135.0", {"start": v(2.85, 11.39) * mm, "end": v(2.85, 8.61) * mm});
            skLineSegment(sketch, "E136.0", {"start": v(7.65, 11.39) * mm, "end": v(5.25, 12.77) * mm});
            skLineSegment(sketch, "E137.0", {"start": v(16, 12.45) * mm, "end": v(16, 10.15) * mm});
            skLineSegment(sketch, "E138.0", {"start": v(16, 10.15) * mm, "end": v(14, 9) * mm});
            skLineSegment(sketch, "E139.0", {"start": v(14, 13.6) * mm, "end": v(16, 12.45) * mm});
            skLineSegment(sketch, "E140.0", {"start": v(7.65, 8.61) * mm, "end": v(7.65, 11.39) * mm});
            skLineSegment(sketch, "E141.0", {"start": v(2.85, 8.61) * mm, "end": v(5.25, 7.23) * mm});
            skLineSegment(sketch, "E142.0", {"start": v(14, 9) * mm, "end": v(12, 10.15) * mm});
            skLineSegment(sketch, "E143.0", {"start": v(37, 12.45) * mm, "end": v(37, 10.15) * mm});
            skLineSegment(sketch, "E144.0", {"start": v(39, 13.6) * mm, "end": v(37, 12.45) * mm});
            skLineSegment(sketch, "E145.0", {"start": v(41, 12.45) * mm, "end": v(39, 13.6) * mm});
            skLineSegment(sketch, "E146.0", {"start": v(41, 10.15) * mm, "end": v(41, 12.45) * mm});
            skSolve(sketch);
        }
        {
            var Q0;
            Q0=makeQuery(id+"F39.imprint","IMPRINT",FACE,{"disambiguationData":[TD([[makeQuery(id+"F39.imprint","IMPRINT",EDGE,{"derivedFrom":sQuery(id+"F39.wireOp",EDGE,"E101.0")}),-1.0]])]});
            var Q1;
            Q1=makeQuery(id+"F39.imprint","IMPRINT",FACE,{"disambiguationData":[TD([[makeQuery(id+"F39.imprint","IMPRINT",EDGE,{"derivedFrom":sQuery(id+"F39.wireOp",EDGE,"E105.0")}),1.0]])]});
            var Q2;
            Q2=makeQuery(id+"F39.imprint","IMPRINT",FACE,{"disambiguationData":[TD([[makeQuery(id+"F39.imprint","IMPRINT",EDGE,{"derivedFrom":sQuery(id+"F39.wireOp",EDGE,"E117.2")}),-1.0]])]});
            var Q3;
            Q3=makeQuery(id+"F39.imprint","IMPRINT",FACE,{"disambiguationData":[TD([[makeQuery(id+"F39.imprint","IMPRINT",EDGE,{"derivedFrom":sQuery(id+"F39.wireOp",EDGE,"E109.0")}),-1.0]])]});
            var Q4;
            Q4=makeQuery(id+"F39.imprint","IMPRINT",FACE,{"disambiguationData":[TD([[makeQuery(id+"F39.imprint","IMPRINT",EDGE,{"derivedFrom":sQuery(id+"F39.wireOp",EDGE,"E115.0")}),1.0]])]});
            var Q5;
            Q5=makeQuery(id+"F39.imprint","IMPRINT",FACE,{"disambiguationData":[TD([[makeQuery(id+"F39.imprint","IMPRINT",EDGE,{"derivedFrom":sQuery(id+"F39.wireOp",EDGE,"E123.0")}),-1.0]])]});
            var Q6;
            Q6=makeQuery(id+"F39.imprint","IMPRINT",FACE,{"disambiguationData":[TD([[makeQuery(id+"F39.imprint","IMPRINT",EDGE,{"derivedFrom":sQuery(id+"F39.wireOp",EDGE,"E100.0")}),1.0]])]});
            var Q7;
            Q7=makeQuery(id+"F39.imprint","IMPRINT",FACE,{"disambiguationData":[TD([[makeQuery(id+"F39.imprint","IMPRINT",EDGE,{"derivedFrom":sQuery(id+"F39.wireOp",EDGE,"E116.0")}),1.0]])]});
            var Q8;
            Q8=makeQuery(id+"F39.imprint","IMPRINT",FACE,{"disambiguationData":[TD([[makeQuery(id+"F39.imprint","IMPRINT",EDGE,{"derivedFrom":sQuery(id+"F39.wireOp",EDGE,"E112.0")}),1.0]])]});
            var Q9;
            Q9=makeQuery(id+"F39.imprint","IMPRINT",FACE,{"disambiguationData":[TD([[makeQuery(id+"F39.imprint","IMPRINT",EDGE,{"derivedFrom":sQuery(id+"F39.wireOp",EDGE,"E108.0")}),1.0]])]});
            extrude(context, id + "F40", {"entities" : qUnion([Q0, Q1, Q2, Q3, Q4, Q5, Q6, Q7, Q8, Q9]), "operationType" : NewBodyOperationType.REMOVE, "oppositeDirection" : true, "depth" : 1 * mm});
        }
        {
            var Q0;
            Q0=makeQuery(id+"F22.boolean.opBoolean","MERGE",FACE,{"derivedFrom":[makeQuery(id+"F3.boolean.opBoolean","MERGE",FACE,{"derivedFrom":[makeQuery(id+"F1.opExtrude","SWEPT_FACE",FACE,{"disambiguationData":[OSD([sQuery(id+"F0.wireOp",EDGE,"E13.top"),sQuery(id+"F0.wireOp",EDGE,"E16")])]}),makeQuery(id+"F3.opExtrude","SWEPT_FACE",FACE,{"disambiguationData":[OSD([sQuery(id+"F2.wireOp",EDGE,"E17.0.2")])]})]}),makeQuery(id+"F22.opExtrude","SWEPT_FACE",FACE,{"disambiguationData":[OSD([sQuery(id+"F21.wireOp",EDGE,"E48")])]})]});
            var sketch = newSketch(context, id + "F41", { "sketchPlane" : qUnion([Q0])});
            skLineSegment(sketch, "E147.0", {"start": v(-57.6, 4.5) * mm, "end": v(-57.6, 16.5) * mm});
            skLineSegment(sketch, "E147.1", {"start": v(-67.4, 4.5) * mm, "end": v(-57.6, 4.5) * mm});
            skLineSegment(sketch, "E147.2", {"start": v(-67.4, 16.5) * mm, "end": v(-67.4, 4.5) * mm});
            skLineSegment(sketch, "E147.3", {"start": v(-57.6, 16.5) * mm, "end": v(-67.4, 16.5) * mm});
            skLineSegment(sketch, "E148.0", {"start": v(-37.34, 5.2) * mm, "end": v(-34.5, 7.27) * mm});
            skLineSegment(sketch, "E148.1", {"start": v(-34.5, 11.8) * mm, "end": v(-50.5, 11.8) * mm});
            skLineSegment(sketch, "E148.2", {"start": v(-50.5, 11.8) * mm, "end": v(-50.5, 7.27) * mm});
            skLineSegment(sketch, "E148.3", {"start": v(-34.5, 7.27) * mm, "end": v(-34.5, 11.8) * mm});
            skLineSegment(sketch, "E148.4", {"start": v(-50.5, 7.27) * mm, "end": v(-47.66, 5.2) * mm});
            skLineSegment(sketch, "E148.5", {"start": v(-47.66, 5.2) * mm, "end": v(-37.34, 5.2) * mm});
            skLineSegment(sketch, "E149.0", {"start": v(-30.15, 11.67) * mm, "end": v(-30.15, 8.33) * mm});
            skLineSegment(sketch, "E149.1", {"start": v(-27.25, 6.65) * mm, "end": v(-24.35, 8.33) * mm});
            skLineSegment(sketch, "E149.2", {"start": v(-24.35, 8.33) * mm, "end": v(-24.35, 11.67) * mm});
            skLineSegment(sketch, "E149.3", {"start": v(-30.15, 8.33) * mm, "end": v(-27.25, 6.65) * mm});
            skLineSegment(sketch, "E149.4", {"start": v(-24.35, 11.67) * mm, "end": v(-27.25, 13.35) * mm});
            skLineSegment(sketch, "E149.5", {"start": v(-27.25, 13.35) * mm, "end": v(-30.15, 11.67) * mm});
            skLineSegment(sketch, "E150.0", {"start": v(1.5, 9.23) * mm, "end": v(1.5, 14.4) * mm});
            skLineSegment(sketch, "E150.1", {"start": v(-23.5, 14.4) * mm, "end": v(-23.5, 9.23) * mm});
            skLineSegment(sketch, "E150.2", {"start": v(-23.5, 9.23) * mm, "end": v(-22.37, 5.6) * mm});
            skLineSegment(sketch, "E150.3", {"start": v(1.5, 14.4) * mm, "end": v(-23.5, 14.4) * mm});
            skLineSegment(sketch, "E150.4", {"start": v(-22.37, 5.6) * mm, "end": v(0.37, 5.6) * mm});
            skLineSegment(sketch, "E150.5", {"start": v(0.37, 5.6) * mm, "end": v(1.5, 9.23) * mm});
            skLineSegment(sketch, "E151.0", {"start": v(8.15, 8.33) * mm, "end": v(8.15, 11.67) * mm});
            skLineSegment(sketch, "E151.1", {"start": v(5.25, 13.35) * mm, "end": v(2.35, 11.67) * mm});
            skLineSegment(sketch, "E151.2", {"start": v(2.35, 11.67) * mm, "end": v(2.35, 8.33) * mm});
            skLineSegment(sketch, "E151.3", {"start": v(8.15, 11.67) * mm, "end": v(5.25, 13.35) * mm});
            skLineSegment(sketch, "E151.4", {"start": v(2.35, 8.33) * mm, "end": v(5.25, 6.65) * mm});
            skLineSegment(sketch, "E151.5", {"start": v(5.25, 6.65) * mm, "end": v(8.15, 8.33) * mm});
            skLineSegment(sketch, "E152.0", {"start": v(16.5, 12.74) * mm, "end": v(14, 14.19) * mm});
            skLineSegment(sketch, "E152.1", {"start": v(11.5, 12.74) * mm, "end": v(11.5, 9.86) * mm});
            skLineSegment(sketch, "E152.2", {"start": v(11.5, 9.86) * mm, "end": v(14, 8.41) * mm});
            skLineSegment(sketch, "E152.3", {"start": v(14, 14.19) * mm, "end": v(11.5, 12.74) * mm});
            skLineSegment(sketch, "E152.4", {"start": v(14, 8.41) * mm, "end": v(16.5, 9.86) * mm});
            skLineSegment(sketch, "E152.5", {"start": v(16.5, 9.86) * mm, "end": v(16.5, 12.74) * mm});
            skLineSegment(sketch, "E153.0", {"start": v(17.74, 14.4) * mm, "end": v(19.44, 5.6) * mm});
            skLineSegment(sketch, "E153.1", {"start": v(35.26, 14.4) * mm, "end": v(17.74, 14.4) * mm});
            skLineSegment(sketch, "E153.2", {"start": v(33.56, 5.6) * mm, "end": v(35.26, 14.4) * mm});
            skLineSegment(sketch, "E153.3", {"start": v(19.44, 5.6) * mm, "end": v(33.56, 5.6) * mm});
            skLineSegment(sketch, "E154.0", {"start": v(39, 14.19) * mm, "end": v(36.5, 12.74) * mm});
            skLineSegment(sketch, "E154.1", {"start": v(36.5, 9.86) * mm, "end": v(39, 8.41) * mm});
            skLineSegment(sketch, "E154.2", {"start": v(39, 8.41) * mm, "end": v(41.5, 9.86) * mm});
            skLineSegment(sketch, "E154.3", {"start": v(36.5, 12.74) * mm, "end": v(36.5, 9.86) * mm});
            skLineSegment(sketch, "E154.4", {"start": v(41.5, 9.86) * mm, "end": v(41.5, 12.74) * mm});
            skLineSegment(sketch, "E154.5", {"start": v(41.5, 12.74) * mm, "end": v(39, 14.19) * mm});
            skCircle(sketch, "E155.0", {"center": v(50.5, 12) * mm, "radius": 3.5 * mm});
            skCircle(sketch, "E156.0", {"center": v(62.5, 12) * mm, "radius": 3.75 * mm});
            skSolve(sketch);
        }
        {
            var Q0;
            Q0 = qSketchRegion(id + "F41", true);
            var Q1;
            Q1=makeQuery(id+"F24.boolean.opBoolean","MERGE",FACE,{"derivedFrom":[makeQuery(id+"F3.opExtrude","SWEPT_FACE",FACE,{"disambiguationData":[OSD([sQuery(id+"F2.wireOp",EDGE,"E18.2")])]}),makeQuery(id+"F24.opExtrude","SWEPT_FACE",FACE,{"disambiguationData":[OSD([sQuery(id+"F23.wireOp",EDGE,"E52.top")])]})]});
            extrude(context, id + "F42", {"entities" : qUnion([Q0]), "operationType" : NewBodyOperationType.REMOVE, "endBound" : BoundingType.UP_TO_SURFACE, "oppositeDirection" : true, "endBoundEntityFace" : qUnion([Q1]), "depth" : 25 * mm});
        }
        {
            var Q0;
            Q0=makeQuery(id+"F26.boolean.opBoolean","MERGE",FACE,{"derivedFrom":[makeQuery(id+"F22.boolean.opBoolean","MERGE",FACE,{"derivedFrom":[makeQuery(id+"F3.opExtrude","CAP_FACE",FACE,{"disambiguationData":[OSD([sQuery(id+"F2.wireOp",EDGE,"E17.0.0"),sQuery(id+"F2.wireOp",EDGE,"E17.0.1"),sQuery(id+"F2.wireOp",EDGE,"E17.0.2"),sQuery(id+"F2.wireOp",EDGE,"E17.0.3"),sQuery(id+"F2.wireOp",EDGE,"E18.0"),sQuery(id+"F2.wireOp",EDGE,"E18.1"),sQuery(id+"F2.wireOp",EDGE,"E18.2"),sQuery(id+"F2.wireOp",EDGE,"E18.3")])],"isStart":false}),makeQuery(id+"F22.opExtrude","CAP_FACE",FACE,{"disambiguationData":[OSD([sQuery(id+"F21.wireOp",EDGE,"E48"),sQuery(id+"F21.wireOp",EDGE,"E49"),sQuery(id+"F21.wireOp",EDGE,"E50"),sQuery(id+"F21.wireOp",EDGE,"E51")])],"isStart":true})]}),makeQuery(id+"F26.opExtrude","CAP_FACE",FACE,{"disambiguationData":[OSD([sQuery(id+"F25.wireOp",EDGE,"E54.bottom"),sQuery(id+"F25.wireOp",EDGE,"E54.top"),sQuery(id+"F25.wireOp",EDGE,"E54.left"),sQuery(id+"F25.wireOp",EDGE,"E54.right")])],"isStart":false})]});
            var sketch = newSketch(context, id + "F43", { "sketchPlane" : qUnion([Q0])});
            skLineSegment(sketch, "E157", {"start": v(96, 44) * mm, "end": v(96, -18.28) * mm, "construction": true});
            skLineSegment(sketch, "E158", {"start": v(55.76, 11) * mm, "end": v(140.45, 11) * mm, "construction": true});
            skLineSegment(sketch, "E159.bottom", {"start": v(118, 33) * mm, "end": v(96, 33) * mm});
            skLineSegment(sketch, "E159.top", {"start": v(118, 11) * mm, "end": v(96, 11) * mm});
            skLineSegment(sketch, "E159.left", {"start": v(118, 33) * mm, "end": v(118, 11) * mm});
            skLineSegment(sketch, "E159.right", {"start": v(96, 33) * mm, "end": v(96, 11) * mm});
            skLineSegment(sketch, "E160.bottom", {"start": v(-137, 33) * mm, "end": v(-159, 33) * mm});
            skLineSegment(sketch, "E160.top", {"start": v(-137, 11) * mm, "end": v(-159, 11) * mm});
            skLineSegment(sketch, "E160.left", {"start": v(-137, 33) * mm, "end": v(-137, 11) * mm});
            skLineSegment(sketch, "E160.right", {"start": v(-159, 33) * mm, "end": v(-159, 11) * mm});
            skSolve(sketch);
        }
        {
            var Q0;
            Q0 = qSketchRegion(id + "F43", true);
            extrude(context, id + "F44", {"entities" : qUnion([Q0]), "operationType" : NewBodyOperationType.REMOVE, "oppositeDirection" : true, "depth" : 12 * mm});
        }
        {
            var Q0;
            {var subQ1=sQuery(id+"F4.wireOp",EDGE,"E22");Q0=makeQuery(id+"F44.boolean.opBoolean","MERGE",FACE,{"derivedFrom":[makeQuery(id+"F7.boolean.opBoolean","SPLIT",FACE,{"disambiguationData":[TD([makeQuery(id+"F1.opExtrude","SWEPT_FACE",FACE,{"disambiguationData":[OSD([sQuery(id+"F0.wireOp",EDGE,"E15")])]})])],"derivedFrom":makeQuery(id+"F5.opExtrude","SWEPT_FACE",FACE,{"disambiguationData":[OSD([subQ1])]})}),makeQuery(id+"F44.opExtrude","CAP_FACE",FACE,{"disambiguationData":[OSD([sQuery(id+"F43.wireOp",EDGE,"E159.bottom"),sQuery(id+"F43.wireOp",EDGE,"E159.top"),sQuery(id+"F43.wireOp",EDGE,"E159.left"),sQuery(id+"F43.wireOp",EDGE,"E159.right")])],"isStart":false})]});}
            var sketch = newSketch(context, id + "F45", { "sketchPlane" : qUnion([Q0])});
            skLineSegment(sketch, "E161.bottom", {"start": v(96, 33) * mm, "end": v(118, 33) * mm});
            skLineSegment(sketch, "E161.top", {"start": v(96, 11) * mm, "end": v(118, 11) * mm});
            skLineSegment(sketch, "E161.left", {"start": v(96, 33) * mm, "end": v(96, 11) * mm});
            skLineSegment(sketch, "E161.right", {"start": v(118, 33) * mm, "end": v(118, 11) * mm});
            skPoint(sketch, "E162.0", {"position": v(-159, 33) * mm});
            skPoint(sketch, "E163.0", {"position": v(-137, 33) * mm});
            skPoint(sketch, "E164.0", {"position": v(-159, 11) * mm});
            skLineSegment(sketch, "E165.bottom", {"start": v(-159, 33) * mm, "end": v(-137, 33) * mm});
            skLineSegment(sketch, "E165.top", {"start": v(-159, 11) * mm, "end": v(-137, 11) * mm});
            skLineSegment(sketch, "E165.left", {"start": v(-159, 33) * mm, "end": v(-159, 11) * mm});
            skLineSegment(sketch, "E165.right", {"start": v(-137, 33) * mm, "end": v(-137, 11) * mm});
            skSolve(sketch);
        }
        {
            var Q0;
            Q0 = qSketchRegion(id + "F45", true);
            extrude(context, id + "F46", {"entities" : qUnion([Q0]), "operationType" : NewBodyOperationType.ADD, "oppositeDirection" : true, "depth" : 2 * mm});
        }
        {
            var Q0;
            Q0=makeQuery(id+"F30.boolean.opBoolean","MERGE",FACE,{"derivedFrom":[makeQuery(id+"F24.boolean.opBoolean","MERGE",FACE,{"derivedFrom":[makeQuery(id+"F1.opExtrude","CAP_FACE",FACE,{"disambiguationData":[OSD([sQuery(id+"F0.wireOp",EDGE,"E1"),sQuery(id+"F0.wireOp",EDGE,"E2"),sQuery(id+"F0.wireOp",EDGE,"E3"),sQuery(id+"F0.wireOp",EDGE,"E4"),sQuery(id+"F0.wireOp",EDGE,"E7.MirrorC"),sQuery(id+"F0.wireOp",EDGE,"E8.MirrorC"),sQuery(id+"F0.wireOp",EDGE,"E13.bottom"),sQuery(id+"F0.wireOp",EDGE,"E13.top"),sQuery(id+"F0.wireOp",EDGE,"E13.left"),sQuery(id+"F0.wireOp",EDGE,"E14"),sQuery(id+"F0.wireOp",EDGE,"E15"),sQuery(id+"F0.wireOp",EDGE,"E16")])],"isStart":false}),makeQuery(id+"F24.opExtrude","CAP_FACE",FACE,{"disambiguationData":[OSD([sQuery(id+"F23.wireOp",EDGE,"E52.bottom"),sQuery(id+"F23.wireOp",EDGE,"E52.top"),sQuery(id+"F23.wireOp",EDGE,"E52.left"),sQuery(id+"F23.wireOp",EDGE,"E52.right")])],"isStart":false})]}),makeQuery(id+"F30.opExtrude","SWEPT_FACE",FACE,{"disambiguationData":[OSD([sQuery(id+"F29.wireOp",EDGE,"E61.1"),sQuery(id+"F29.wireOp",EDGE,"E63")])]})]});
            var sketch = newSketch(context, id + "F47", { "sketchPlane" : qUnion([Q0])});
            skCircle(sketch, "E166", {"center": v(107, 19) * mm, "radius": 7.5 * mm});
            skCircle(sketch, "E167", {"center": v(107, 19) * mm, "radius": 5 * mm});
            skCircle(sketch, "E168", {"center": v(-147.5, 19) * mm, "radius": 5 * mm});
            skCircle(sketch, "E169", {"center": v(-147.5, 19) * mm, "radius": 5.5 * mm});
            skSolve(sketch);
        }
        {
            var Q0;
            Q0=makeQuery(id+"F47.imprint","IMPRINT",FACE,{"disambiguationData":[TD([[makeQuery(id+"F47.imprint","IMPRINT",EDGE,{"derivedFrom":sQuery(id+"F47.wireOp",EDGE,"E168")}),-1.0]])]});
            var Q1;
            Q1=makeQuery(id+"F47.imprint","IMPRINT",FACE,{"disambiguationData":[TD([[makeQuery(id+"F47.imprint","IMPRINT",EDGE,{"derivedFrom":sQuery(id+"F47.wireOp",EDGE,"E166")}),1.0]])]});
            var Q2;
            {var subQ1=sQuery(id+"F4.wireOp",EDGE,"E22");Q2=makeQuery(id+"F46.boolean.opBoolean","MERGE",FACE,{"derivedFrom":[makeQuery(id+"F44.boolean.opBoolean","MERGE",FACE,{"derivedFrom":[makeQuery(id+"F7.boolean.opBoolean","SPLIT",FACE,{"disambiguationData":[TD([makeQuery(id+"F1.opExtrude","SWEPT_FACE",FACE,{"disambiguationData":[OSD([sQuery(id+"F0.wireOp",EDGE,"E13.left")])]})])],"derivedFrom":makeQuery(id+"F5.opExtrude","SWEPT_FACE",FACE,{"disambiguationData":[OSD([subQ1])]})}),makeQuery(id+"F44.opExtrude","CAP_FACE",FACE,{"disambiguationData":[OSD([sQuery(id+"F43.wireOp",EDGE,"E160.bottom"),sQuery(id+"F43.wireOp",EDGE,"E160.top"),sQuery(id+"F43.wireOp",EDGE,"E160.left"),sQuery(id+"F43.wireOp",EDGE,"E160.right")])],"isStart":false})]}),makeQuery(id+"F46.opExtrude","CAP_FACE",FACE,{"disambiguationData":[OSD([sQuery(id+"F45.wireOp",EDGE,"E165.bottom"),sQuery(id+"F45.wireOp",EDGE,"E165.top"),sQuery(id+"F45.wireOp",EDGE,"E165.left"),sQuery(id+"F45.wireOp",EDGE,"E165.right")])],"isStart":true})]});}
            extrude(context, id + "F48", {"entities" : qUnion([Q0, Q1]), "operationType" : NewBodyOperationType.ADD, "endBound" : BoundingType.UP_TO_SURFACE, "endBoundEntityFace" : qUnion([Q2]), "depth" : 14 * mm});
        }
        {
            var Q0;
            {var subQ0=sQuery(id+"F45.wireOp",EDGE,"E161.top");var subQ1=sQuery(id+"F45.wireOp",EDGE,"E161.left");Q0=makeQuery(id+"F48.boolean.opBoolean","SPLIT",FACE,{"disambiguationData":[TD([makeQuery(id+"F3.opExtrude","SWEPT_FACE",FACE,{"disambiguationData":[OSD([sQuery(id+"F2.wireOp",EDGE,"E18.0")])]})])],"derivedFrom":makeQuery(id+"F46.opExtrude","CAP_FACE",FACE,{"disambiguationData":[OSD([sQuery(id+"F45.wireOp",EDGE,"E161.bottom"),subQ0,subQ1,sQuery(id+"F45.wireOp",EDGE,"E161.right")])],"isStart":false})});}
            var sketch = newSketch(context, id + "F49", { "sketchPlane" : qUnion([Q0])});
            skPoint(sketch, "E170.0", {"position": v(96, -33) * mm});
            skPoint(sketch, "E171.0", {"position": v(118, -11) * mm});
            skLineSegment(sketch, "E172.bottom", {"start": v(118, -11) * mm, "end": v(94, -11) * mm});
            skLineSegment(sketch, "E172.top", {"start": v(118, -9) * mm, "end": v(94, -9) * mm});
            skLineSegment(sketch, "E172.left", {"start": v(118, -11) * mm, "end": v(118, -9) * mm});
            skLineSegment(sketch, "E172.right", {"start": v(94, -11) * mm, "end": v(94, -9) * mm});
            skLineSegment(sketch, "E173.bottom", {"start": v(96, -33) * mm, "end": v(94, -33) * mm});
            skLineSegment(sketch, "E173.top", {"start": v(96, -9) * mm, "end": v(94, -9) * mm});
            skLineSegment(sketch, "E173.left", {"start": v(96, -33) * mm, "end": v(96, -9) * mm});
            skLineSegment(sketch, "E173.right", {"start": v(94, -33) * mm, "end": v(94, -9) * mm});
            skPoint(sketch, "E174.0", {"position": v(-137, -33) * mm});
            skPoint(sketch, "E175.0", {"position": v(-159, -11) * mm});
            skLineSegment(sketch, "E176.bottom", {"start": v(-159, -11) * mm, "end": v(-135, -11) * mm});
            skLineSegment(sketch, "E176.top", {"start": v(-159, -9) * mm, "end": v(-135, -9) * mm});
            skLineSegment(sketch, "E176.left", {"start": v(-159, -11) * mm, "end": v(-159, -9) * mm});
            skLineSegment(sketch, "E176.right", {"start": v(-135, -11) * mm, "end": v(-135, -9) * mm});
            skLineSegment(sketch, "E177.bottom", {"start": v(-137, -33) * mm, "end": v(-135, -33) * mm});
            skLineSegment(sketch, "E177.top", {"start": v(-137, -9) * mm, "end": v(-135, -9) * mm});
            skLineSegment(sketch, "E177.left", {"start": v(-137, -33) * mm, "end": v(-137, -9) * mm});
            skLineSegment(sketch, "E177.right", {"start": v(-135, -33) * mm, "end": v(-135, -9) * mm});
            skSolve(sketch);
        }
        {
            var Q0;
            Q0 = qSketchRegion(id + "F49", true);
            var Q1;
            Q1=makeQuery(id+"F26.boolean.opBoolean","MERGE",FACE,{"derivedFrom":[makeQuery(id+"F22.boolean.opBoolean","MERGE",FACE,{"derivedFrom":[makeQuery(id+"F3.opExtrude","CAP_FACE",FACE,{"disambiguationData":[OSD([sQuery(id+"F2.wireOp",EDGE,"E17.0.0"),sQuery(id+"F2.wireOp",EDGE,"E17.0.1"),sQuery(id+"F2.wireOp",EDGE,"E17.0.2"),sQuery(id+"F2.wireOp",EDGE,"E17.0.3"),sQuery(id+"F2.wireOp",EDGE,"E18.0"),sQuery(id+"F2.wireOp",EDGE,"E18.1"),sQuery(id+"F2.wireOp",EDGE,"E18.2"),sQuery(id+"F2.wireOp",EDGE,"E18.3")])],"isStart":false}),makeQuery(id+"F22.opExtrude","CAP_FACE",FACE,{"disambiguationData":[OSD([sQuery(id+"F21.wireOp",EDGE,"E48"),sQuery(id+"F21.wireOp",EDGE,"E49"),sQuery(id+"F21.wireOp",EDGE,"E50"),sQuery(id+"F21.wireOp",EDGE,"E51")])],"isStart":true})]}),makeQuery(id+"F26.opExtrude","CAP_FACE",FACE,{"disambiguationData":[OSD([sQuery(id+"F25.wireOp",EDGE,"E54.bottom"),sQuery(id+"F25.wireOp",EDGE,"E54.top"),sQuery(id+"F25.wireOp",EDGE,"E54.left"),sQuery(id+"F25.wireOp",EDGE,"E54.right")])],"isStart":false})]});
            extrude(context, id + "F50", {"entities" : qUnion([Q0]), "operationType" : NewBodyOperationType.ADD, "endBound" : BoundingType.UP_TO_SURFACE, "oppositeDirection" : true, "endBoundEntityFace" : qUnion([Q1]), "depth" : 25 * mm});
        }
        {
            var Q0;
            {var subQ1=sQuery(id+"F4.wireOp",EDGE,"E22");Q0=makeQuery(id+"F46.boolean.opBoolean","MERGE",FACE,{"derivedFrom":[makeQuery(id+"F44.boolean.opBoolean","MERGE",FACE,{"derivedFrom":[makeQuery(id+"F7.boolean.opBoolean","SPLIT",FACE,{"disambiguationData":[TD([makeQuery(id+"F1.opExtrude","SWEPT_FACE",FACE,{"disambiguationData":[OSD([sQuery(id+"F0.wireOp",EDGE,"E15")])]})])],"derivedFrom":makeQuery(id+"F5.opExtrude","SWEPT_FACE",FACE,{"disambiguationData":[OSD([subQ1])]})}),makeQuery(id+"F44.opExtrude","CAP_FACE",FACE,{"disambiguationData":[OSD([sQuery(id+"F43.wireOp",EDGE,"E159.bottom"),sQuery(id+"F43.wireOp",EDGE,"E159.top"),sQuery(id+"F43.wireOp",EDGE,"E159.left"),sQuery(id+"F43.wireOp",EDGE,"E159.right")])],"isStart":false})]}),makeQuery(id+"F46.opExtrude","CAP_FACE",FACE,{"disambiguationData":[OSD([sQuery(id+"F45.wireOp",EDGE,"E161.bottom"),sQuery(id+"F45.wireOp",EDGE,"E161.top"),sQuery(id+"F45.wireOp",EDGE,"E161.left"),sQuery(id+"F45.wireOp",EDGE,"E161.right")])],"isStart":true})]});}
            var sketch = newSketch(context, id + "F51", { "sketchPlane" : qUnion([Q0])});
            skCircle(sketch, "E178.0", {"center": v(107, 19) * mm, "radius": 5 * mm});
            skCircle(sketch, "E179.0", {"center": v(-147.5, 19) * mm, "radius": 5 * mm});
            skSolve(sketch);
        }
        {
            var Q0;
            Q0 = qSketchRegion(id + "F51", true);
            var Q1;
            {var subQ0=sQuery(id+"F23.wireOp",EDGE,"E52.right");var subQ1=sQuery(id+"F23.wireOp",EDGE,"E52.bottom");var subQ2=sQuery(id+"F23.wireOp",EDGE,"E52.top");Q1=makeQuery(id+"F48.boolean.opBoolean","SPLIT",FACE,{"disambiguationData":[TD([makeQuery(id+"F3.opExtrude","SWEPT_FACE",FACE,{"disambiguationData":[OSD([sQuery(id+"F2.wireOp",EDGE,"E18.0")])]})])],"derivedFrom":makeQuery(id+"F30.boolean.opBoolean","MERGE",FACE,{"derivedFrom":[makeQuery(id+"F24.boolean.opBoolean","MERGE",FACE,{"derivedFrom":[makeQuery(id+"F1.opExtrude","CAP_FACE",FACE,{"disambiguationData":[OSD([sQuery(id+"F0.wireOp",EDGE,"E1"),sQuery(id+"F0.wireOp",EDGE,"E2"),sQuery(id+"F0.wireOp",EDGE,"E3"),sQuery(id+"F0.wireOp",EDGE,"E4"),sQuery(id+"F0.wireOp",EDGE,"E7.MirrorC"),sQuery(id+"F0.wireOp",EDGE,"E8.MirrorC"),sQuery(id+"F0.wireOp",EDGE,"E13.bottom"),sQuery(id+"F0.wireOp",EDGE,"E13.top"),sQuery(id+"F0.wireOp",EDGE,"E13.left"),sQuery(id+"F0.wireOp",EDGE,"E14"),sQuery(id+"F0.wireOp",EDGE,"E15"),sQuery(id+"F0.wireOp",EDGE,"E16")])],"isStart":false}),makeQuery(id+"F24.opExtrude","CAP_FACE",FACE,{"disambiguationData":[OSD([subQ1,subQ2,sQuery(id+"F23.wireOp",EDGE,"E52.left"),subQ0])],"isStart":false})]}),makeQuery(id+"F30.opExtrude","SWEPT_FACE",FACE,{"disambiguationData":[OSD([sQuery(id+"F29.wireOp",EDGE,"E61.1"),sQuery(id+"F29.wireOp",EDGE,"E63")])]})]})});}
            extrude(context, id + "F52", {"entities" : qUnion([Q0]), "operationType" : NewBodyOperationType.REMOVE, "endBound" : BoundingType.UP_TO_SURFACE, "oppositeDirection" : true, "endBoundEntityFace" : qUnion([Q1]), "depth" : 25 * mm});
        }
        {
            var Q0;
            {var subQ0=sQuery(id+"F23.wireOp",EDGE,"E52.right");var subQ1=sQuery(id+"F23.wireOp",EDGE,"E52.bottom");var subQ2=sQuery(id+"F23.wireOp",EDGE,"E52.top");Q0=makeQuery(id+"F48.boolean.opBoolean","SPLIT",FACE,{"disambiguationData":[TD([makeQuery(id+"F3.opExtrude","SWEPT_FACE",FACE,{"disambiguationData":[OSD([sQuery(id+"F2.wireOp",EDGE,"E18.0")])]})])],"derivedFrom":makeQuery(id+"F30.boolean.opBoolean","MERGE",FACE,{"derivedFrom":[makeQuery(id+"F24.boolean.opBoolean","MERGE",FACE,{"derivedFrom":[makeQuery(id+"F1.opExtrude","CAP_FACE",FACE,{"disambiguationData":[OSD([sQuery(id+"F0.wireOp",EDGE,"E1"),sQuery(id+"F0.wireOp",EDGE,"E2"),sQuery(id+"F0.wireOp",EDGE,"E3"),sQuery(id+"F0.wireOp",EDGE,"E4"),sQuery(id+"F0.wireOp",EDGE,"E7.MirrorC"),sQuery(id+"F0.wireOp",EDGE,"E8.MirrorC"),sQuery(id+"F0.wireOp",EDGE,"E13.bottom"),sQuery(id+"F0.wireOp",EDGE,"E13.top"),sQuery(id+"F0.wireOp",EDGE,"E13.left"),sQuery(id+"F0.wireOp",EDGE,"E14"),sQuery(id+"F0.wireOp",EDGE,"E15"),sQuery(id+"F0.wireOp",EDGE,"E16")])],"isStart":false}),makeQuery(id+"F24.opExtrude","CAP_FACE",FACE,{"disambiguationData":[OSD([subQ1,subQ2,sQuery(id+"F23.wireOp",EDGE,"E52.left"),subQ0])],"isStart":false})]}),makeQuery(id+"F30.opExtrude","SWEPT_FACE",FACE,{"disambiguationData":[OSD([sQuery(id+"F29.wireOp",EDGE,"E61.1"),sQuery(id+"F29.wireOp",EDGE,"E63")])]})]})});}
            var sketch = newSketch(context, id + "F53", { "sketchPlane" : qUnion([Q0])});
            skCircle(sketch, "E180.0", {"center": v(107, 19) * mm, "radius": 7.5 * mm, "construction": true});
            skLineSegment(sketch, "E181", {"start": v(107, 19) * mm, "end": v(110.75, 12.5) * mm});
            skLineSegment(sketch, "E182", {"start": v(107, 19) * mm, "end": v(100.5, 22.75) * mm});
            skArc(sketch, "E183", {"start": v(100.5, 22.75) * mm, "mid": v(101.7, 13.7) * mm, "end": v(110.75, 12.5) * mm});
            skLineSegment(sketch, "E184", {"start": v(93.99, 19) * mm, "end": v(107, 19) * mm, "construction": true});
            skLineSegment(sketch, "E185", {"start": v(107, 19) * mm, "end": v(107, 5.18) * mm, "construction": true});
            skLineSegment(sketch, "E186", {"start": v(-147.5, 19) * mm, "end": v(-108.61, 19) * mm, "construction": true});
            skLineSegment(sketch, "E187", {"start": v(-147.5, 19) * mm, "end": v(-147.5, 0) * mm, "construction": true});
            skLineSegment(sketch, "E188", {"start": v(-147.5, 19) * mm, "end": v(-157.36, 1.93) * mm});
            skLineSegment(sketch, "E189", {"start": v(-147.5, 19) * mm, "end": v(-131.34, 28.33) * mm});
            skArc(sketch, "E190.0", {"start": v(-145, 23.33) * mm, "mid": v(-151.04, 15.46) * mm, "end": v(-143.17, 21.5) * mm});
            skArc(sketch, "E191.0", {"start": v(-144.75, 23.76) * mm, "mid": v(-151.39, 15.11) * mm, "end": v(-142.74, 21.75) * mm});
            skSolve(sketch);
        }
        {
            var Q0;
            Q0 = qSketchRegion(id + "F53", true);
            extrude(context, id + "F54", {"entities" : qUnion([Q0]), "operationType" : NewBodyOperationType.REMOVE, "depth" : 8 * mm});
        }
        {
            var Q0;
            {var subQ1=sQuery(id+"F21.wireOp",EDGE,"E50");var subQ2=sQuery(id+"F25.wireOp",EDGE,"E54.left");var subQ3=sQuery(id+"F2.wireOp",EDGE,"E17.0.0");var subQ4=sQuery(id+"F25.wireOp",EDGE,"E54.right");var subQ5=sQuery(id+"F2.wireOp",EDGE,"E18.0");var subQ7=sQuery(id+"F21.wireOp",EDGE,"E49");var subQ8=sQuery(id+"F21.wireOp",EDGE,"E48");var subQ9=sQuery(id+"F2.wireOp",EDGE,"E18.2");var subQ10=sQuery(id+"F2.wireOp",EDGE,"E18.1");var subQ11=sQuery(id+"F2.wireOp",EDGE,"E17.0.3");var subQ12=sQuery(id+"F2.wireOp",EDGE,"E17.0.2");var subQ13=makeQuery(id+"F26.boolean.opBoolean","MERGE",FACE,{"derivedFrom":[makeQuery(id+"F22.boolean.opBoolean","MERGE",FACE,{"derivedFrom":[makeQuery(id+"F3.opExtrude","CAP_FACE",FACE,{"disambiguationData":[OSD([subQ3,sQuery(id+"F2.wireOp",EDGE,"E17.0.1"),subQ12,subQ11,subQ5,subQ10,subQ9,sQuery(id+"F2.wireOp",EDGE,"E18.3")])],"isStart":false}),makeQuery(id+"F22.opExtrude","CAP_FACE",FACE,{"disambiguationData":[OSD([subQ8,subQ7,subQ1,sQuery(id+"F21.wireOp",EDGE,"E51")])],"isStart":true})]}),makeQuery(id+"F26.opExtrude","CAP_FACE",FACE,{"disambiguationData":[OSD([sQuery(id+"F25.wireOp",EDGE,"E54.bottom"),sQuery(id+"F25.wireOp",EDGE,"E54.top"),subQ2,subQ4])],"isStart":false})]});Q0=makeQuery(id+"F50.boolean.opBoolean","MERGE",FACE,{"derivedFrom":[makeQuery(id+"F44.boolean.opBoolean","SPLIT",FACE,{"disambiguationData":[TD([makeQuery(id+"F1.opExtrude","SWEPT_FACE",FACE,{"disambiguationData":[OSD([sQuery(id+"F0.wireOp",EDGE,"E15")])]})])],"derivedFrom":subQ13}),makeQuery(id+"F44.boolean.opBoolean","SPLIT",FACE,{"disambiguationData":[TD([makeQuery(id+"F3.opExtrude","SWEPT_FACE",FACE,{"disambiguationData":[OSD([subQ3])]})])],"derivedFrom":subQ13}),makeQuery(id+"F50.opExtrude","CAP_FACE",FACE,{"disambiguationData":[OSD([sQuery(id+"F49.wireOp",EDGE,"E172.bottom"),sQuery(id+"F49.wireOp",EDGE,"E172.top"),sQuery(id+"F49.wireOp",EDGE,"E172.left"),sQuery(id+"F49.wireOp",EDGE,"E173.bottom"),sQuery(id+"F49.wireOp",EDGE,"E173.top"),sQuery(id+"F49.wireOp",EDGE,"E173.left"),sQuery(id+"F49.wireOp",EDGE,"E173.right")])],"isStart":false}),makeQuery(id+"F50.opExtrude","CAP_FACE",FACE,{"disambiguationData":[OSD([sQuery(id+"F49.wireOp",EDGE,"E176.bottom"),sQuery(id+"F49.wireOp",EDGE,"E176.top"),sQuery(id+"F49.wireOp",EDGE,"E176.left"),sQuery(id+"F49.wireOp",EDGE,"E177.bottom"),sQuery(id+"F49.wireOp",EDGE,"E177.top"),sQuery(id+"F49.wireOp",EDGE,"E177.left"),sQuery(id+"F49.wireOp",EDGE,"E177.right")])],"isStart":false})]});}
            var sketch = newSketch(context, id + "F55", { "sketchPlane" : qUnion([Q0])});
            skLineSegment(sketch, "E192.bottom", {"start": v(-157, 9) * mm, "end": v(-152, 9) * mm});
            skLineSegment(sketch, "E192.top", {"start": v(-157, 4) * mm, "end": v(-152, 4) * mm});
            skLineSegment(sketch, "E192.left", {"start": v(-157, 9) * mm, "end": v(-157, 4) * mm});
            skLineSegment(sketch, "E192.right", {"start": v(-152, 9) * mm, "end": v(-152, 4) * mm});
            skLineSegment(sketch, "E193.bottom", {"start": v(-135, 31) * mm, "end": v(-130, 31) * mm});
            skLineSegment(sketch, "E193.top", {"start": v(-135, 26) * mm, "end": v(-130, 26) * mm});
            skLineSegment(sketch, "E193.left", {"start": v(-135, 31) * mm, "end": v(-135, 26) * mm});
            skLineSegment(sketch, "E193.right", {"start": v(-130, 31) * mm, "end": v(-130, 26) * mm});
            skLineSegment(sketch, "E194.bottom", {"start": v(-157, -29) * mm, "end": v(-152, -29) * mm});
            skLineSegment(sketch, "E194.top", {"start": v(-157, -24) * mm, "end": v(-152, -24) * mm});
            skLineSegment(sketch, "E194.left", {"start": v(-157, -29) * mm, "end": v(-157, -24) * mm});
            skLineSegment(sketch, "E194.right", {"start": v(-152, -29) * mm, "end": v(-152, -24) * mm});
            skLineSegment(sketch, "E195.bottom", {"start": v(116, -29) * mm, "end": v(111, -29) * mm});
            skLineSegment(sketch, "E195.top", {"start": v(116, -24) * mm, "end": v(111, -24) * mm});
            skLineSegment(sketch, "E195.left", {"start": v(116, -29) * mm, "end": v(116, -24) * mm});
            skLineSegment(sketch, "E195.right", {"start": v(111, -29) * mm, "end": v(111, -24) * mm});
            skLineSegment(sketch, "E196.bottom", {"start": v(116, 9) * mm, "end": v(111, 9) * mm});
            skLineSegment(sketch, "E196.top", {"start": v(116, 4) * mm, "end": v(111, 4) * mm});
            skLineSegment(sketch, "E196.left", {"start": v(116, 9) * mm, "end": v(116, 4) * mm});
            skLineSegment(sketch, "E196.right", {"start": v(111, 9) * mm, "end": v(111, 4) * mm});
            skLineSegment(sketch, "E197.bottom", {"start": v(94, 31) * mm, "end": v(89, 31) * mm});
            skLineSegment(sketch, "E197.top", {"start": v(94, 26) * mm, "end": v(89, 26) * mm});
            skLineSegment(sketch, "E197.left", {"start": v(94, 31) * mm, "end": v(94, 26) * mm});
            skLineSegment(sketch, "E197.right", {"start": v(89, 31) * mm, "end": v(89, 26) * mm});
            skSolve(sketch);
        }
        {
            var Q0;
            Q0 = qSketchRegion(id + "F55", true);
            var Q1;
            {var subQ0=sQuery(id+"F23.wireOp",EDGE,"E52.right");var subQ1=sQuery(id+"F23.wireOp",EDGE,"E52.top");var subQ2=sQuery(id+"F23.wireOp",EDGE,"E52.bottom");var subQ3=makeQuery(id+"F30.boolean.opBoolean","MERGE",FACE,{"derivedFrom":[makeQuery(id+"F24.boolean.opBoolean","MERGE",FACE,{"derivedFrom":[makeQuery(id+"F1.opExtrude","CAP_FACE",FACE,{"disambiguationData":[OSD([sQuery(id+"F0.wireOp",EDGE,"E1"),sQuery(id+"F0.wireOp",EDGE,"E2"),sQuery(id+"F0.wireOp",EDGE,"E3"),sQuery(id+"F0.wireOp",EDGE,"E4"),sQuery(id+"F0.wireOp",EDGE,"E7.MirrorC"),sQuery(id+"F0.wireOp",EDGE,"E8.MirrorC"),sQuery(id+"F0.wireOp",EDGE,"E13.bottom"),sQuery(id+"F0.wireOp",EDGE,"E13.top"),sQuery(id+"F0.wireOp",EDGE,"E13.left"),sQuery(id+"F0.wireOp",EDGE,"E14"),sQuery(id+"F0.wireOp",EDGE,"E15"),sQuery(id+"F0.wireOp",EDGE,"E16")])],"isStart":false}),makeQuery(id+"F24.opExtrude","CAP_FACE",FACE,{"disambiguationData":[OSD([subQ2,subQ1,sQuery(id+"F23.wireOp",EDGE,"E52.left"),subQ0])],"isStart":false})]}),makeQuery(id+"F30.opExtrude","SWEPT_FACE",FACE,{"disambiguationData":[OSD([sQuery(id+"F29.wireOp",EDGE,"E61.1"),sQuery(id+"F29.wireOp",EDGE,"E63")])]})]});Q1=makeQuery(id+"F54.boolean.opBoolean","MERGE",FACE,{"derivedFrom":[makeQuery(id+"F48.boolean.opBoolean","SPLIT",FACE,{"disambiguationData":[TD([makeQuery(id+"F3.opExtrude","SWEPT_FACE",FACE,{"disambiguationData":[OSD([sQuery(id+"F2.wireOp",EDGE,"E18.0")])]})])],"derivedFrom":subQ3}),makeQuery(id+"F48.boolean.opBoolean","SPLIT",FACE,{"disambiguationData":[TD([makeQuery(id+"F48.opExtrude","SWEPT_FACE",FACE,{"disambiguationData":[OSD([sQuery(id+"F47.wireOp",EDGE,"E167")])]})])],"derivedFrom":subQ3}),makeQuery(id+"F48.boolean.opBoolean","SPLIT",FACE,{"disambiguationData":[TD([makeQuery(id+"F48.opExtrude","SWEPT_FACE",FACE,{"disambiguationData":[OSD([sQuery(id+"F47.wireOp",EDGE,"E168")])]})])],"derivedFrom":subQ3}),makeQuery(id+"F54.opExtrude","CAP_FACE",FACE,{"disambiguationData":[OSD([sQuery(id+"F53.wireOp",EDGE,"E181"),sQuery(id+"F53.wireOp",EDGE,"E182"),sQuery(id+"F53.wireOp",EDGE,"E183")])],"isStart":true}),makeQuery(id+"F54.opExtrude","CAP_FACE",FACE,{"disambiguationData":[OSD([sQuery(id+"F53.wireOp",EDGE,"E188"),sQuery(id+"F53.wireOp",EDGE,"E189"),sQuery(id+"F53.wireOp",EDGE,"E191.0")])],"isStart":true})]});}
            extrude(context, id + "F56", {"entities" : qUnion([Q0]), "operationType" : NewBodyOperationType.ADD, "endBound" : BoundingType.UP_TO_SURFACE, "oppositeDirection" : true, "endBoundEntityFace" : qUnion([Q1]), "depth" : 25 * mm});
        }
    });
